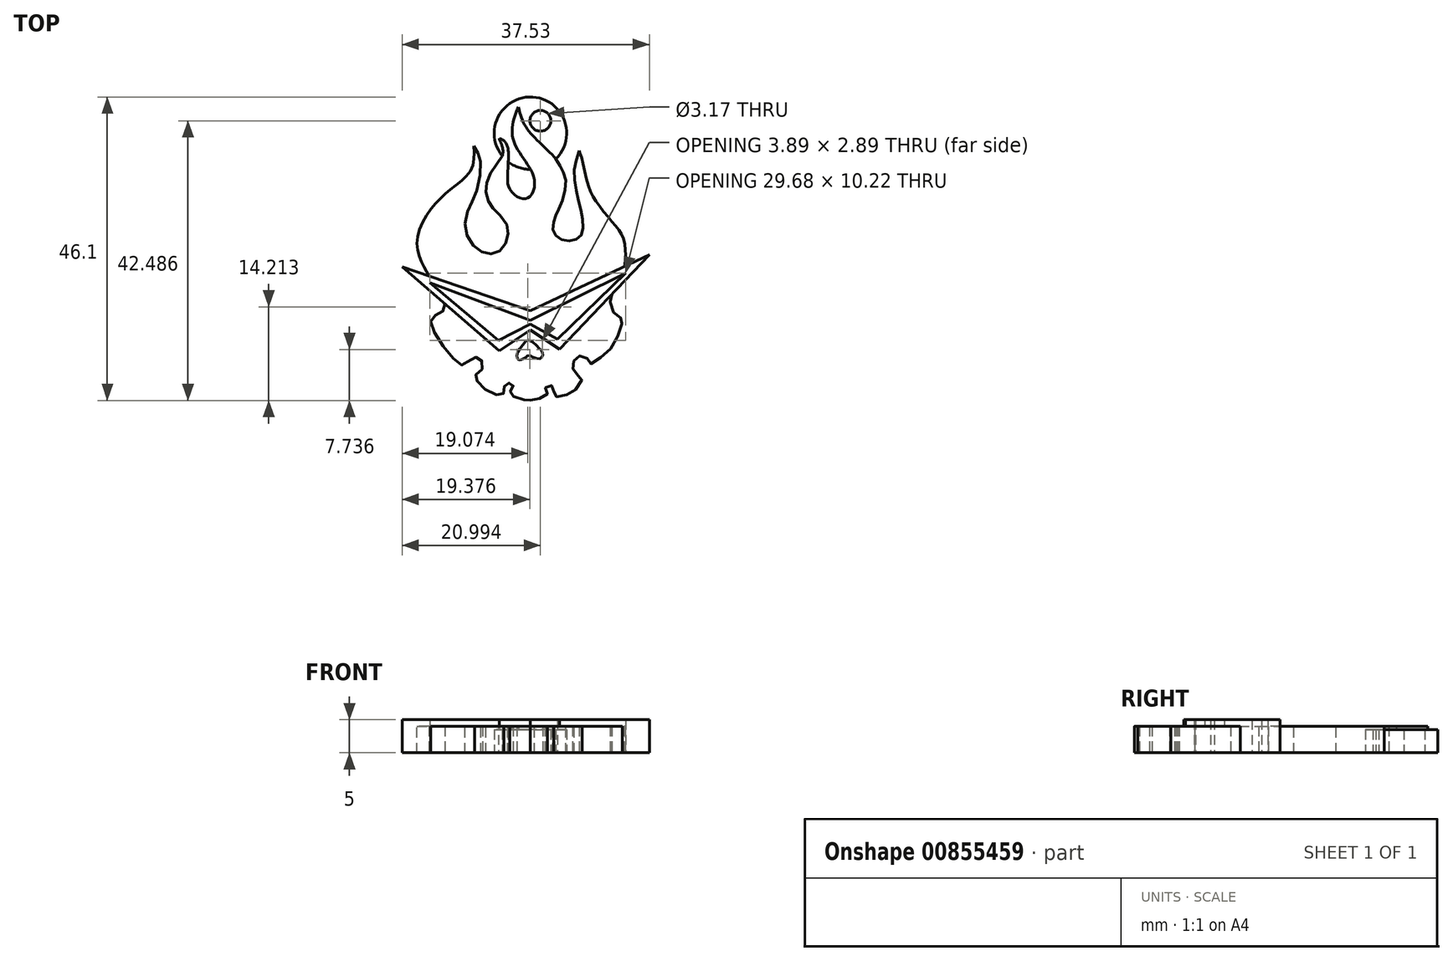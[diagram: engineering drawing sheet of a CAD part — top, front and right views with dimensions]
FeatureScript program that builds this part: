
annotation { "Feature Type Name" : "Feature", "Feature Type Description" : "" }
export const myFeature = defineFeature(function(context is Context, id is Id, definition is map)
    precondition{}
    {
        {
            var Q0;
            Q0=qCreatedBy(makeId("Top.planeOp"),FACE);
            var sketch = newSketch(context, id + "F0", { "sketchPlane" : qUnion([Q0])});
            skLineSegment(sketch, "E0", {"start": v(-8.05, -8.35) * mm, "end": v(-27.53, -1.72) * mm});
            skLineSegment(sketch, "E1", {"start": v(-27.53, -1.72) * mm, "end": v(-12.8, -14.5) * mm});
            skLineSegment(sketch, "E2", {"start": v(-12.8, -14.5) * mm, "end": v(-8.05, -11.32) * mm});
            skLineSegment(sketch, "E3", {"start": v(-8.05, -8.35) * mm, "end": v(10, 0.13) * mm});
            skLineSegment(sketch, "E4", {"start": v(10, 0.13) * mm, "end": v(-3.66, -14.25) * mm});
            skLineSegment(sketch, "E5", {"start": v(-3.66, -14.25) * mm, "end": v(-8.05, -11.32) * mm});
            skFitSpline(sketch, "E6", {"points": [v(-21.02, -7.37) * mm, v(-21.26, -8.4) * mm, v(-22.48, -9.07) * mm, v(-23.16, -9.89) * mm, v(-22.12, -12.56) * mm, v(-19.3, -16.06) * mm, v(-18.22, -16.65) * mm, v(-17.22, -15.78) * mm, v(-15.86, -15.51) * mm, v(-15.36, -16.33) * mm, v(-15.59, -17.55) * mm, v(-16.5, -18.28) * mm, v(-16, -19.23) * mm, v(-13.82, -20.96) * mm, v(-12.19, -21.05) * mm, v(-12.13, -20.46) * mm, v(-11.8, -19.54) * mm, v(-11.21, -19.35) * mm, v(-10.74, -19.62) * mm, v(-10.74, -20.15) * mm, v(-11.2, -20.78) * mm, v(-10.5, -21.49) * mm, v(-8.56, -22) * mm, v(-8.05, -21.98) * mm], "startDerivative": vector(-0.52, -28.52) * mm, "endDerivative": vector(14.8, 2.02) * mm});
            skFitSpline(sketch, "E7", {"points": [v(-8.05, -21.98) * mm, v(-6.85, -21.76) * mm, v(-5.49, -21.08) * mm, v(-5.8, -20.57) * mm, v(-5.6, -19.83) * mm, v(-4.9, -19.7) * mm, v(-4.42, -20.33) * mm, v(-4.53, -21.38) * mm, v(-3.74, -21.35) * mm, v(-2.1, -20.95) * mm, v(-0.78, -19.82) * mm, v(-0.22, -18.5) * mm, v(-0.88, -18.26) * mm, v(-1.58, -17.23) * mm, v(-1.56, -16.25) * mm, v(-0.93, -15.4) * mm, v(-0.19, -15.23) * mm, v(0.69, -15.8) * mm, v(1.01, -16.42) * mm, v(2.64, -15.46) * mm, v(4.56, -13.53) * mm, v(5.74, -10.62) * mm, v(5.84, -9.6) * mm, v(5.46, -9.38) * mm, v(4.38, -8.31) * mm, v(4.07, -6.61) * mm, v(4.29, -5.88) * mm], "startDerivative": vector(26.47, 3.3) * mm, "endDerivative": vector(8.6, 20.3) * mm});
            skFitSpline(sketch, "E8", {"points": [v(-23.45, -3.1) * mm, v(-24.64, -0.81) * mm, v(-25.22, 2.75) * mm, v(-22.84, 7.46) * mm, v(-19.9, 10.25) * mm, v(-17.04, 13.1) * mm, v(-16.65, 16.64) * mm], "startDerivative": vector(-9.07, 15.68) * mm, "endDerivative": vector(-1.26, 23.14) * mm});
            skFitSpline(sketch, "E9", {"points": [v(-16.65, 16.64) * mm, v(-16, 15.52) * mm, v(-15.6, 13.78) * mm, v(-16.4, 9.36) * mm, v(-17.39, 7.27) * mm, v(-18, 4.38) * mm, v(-17, 1.88) * mm, v(-15.27, 0.47) * mm, v(-13.57, 0.31) * mm, v(-12.1, 1.34) * mm, v(-11.49, 3) * mm, v(-11.68, 4.77) * mm, v(-13.22, 6.66) * mm, v(-14.18, 7.78) * mm, v(-14.76, 9.36) * mm, v(-14.7, 11.09) * mm, v(-13.76, 13.1) * mm, v(-12.45, 14.84) * mm, v(-12.26, 16.22) * mm, v(-12.8, 17.76) * mm], "startDerivative": vector(16.1, -26.15) * mm, "endDerivative": vector(-14.54, 32.83) * mm});
            skFitSpline(sketch, "E10", {"points": [v(-12.8, 17.76) * mm, v(-12.17, 17.54) * mm, v(-11.58, 16.64) * mm, v(-11.4, 15.18) * mm, v(-11.52, 11.79) * mm, v(-11.36, 10.47) * mm, v(-10.43, 9.23) * mm, v(-9.14, 8.64) * mm, v(-8.3, 8.84) * mm, v(-7.55, 9.97) * mm, v(-7.55, 11.92) * mm, v(-8.55, 13.9) * mm, v(-10.27, 16.64) * mm, v(-10.84, 18.66) * mm, v(-10.52, 20.93) * mm, v(-9.89, 22.56) * mm], "startDerivative": vector(15.58, -2.77) * mm, "endDerivative": vector(10.1, 22.63) * mm});
            skFitSpline(sketch, "E11", {"points": [v(-9.89, 22.56) * mm, v(-9.55, 21.27) * mm, v(-8.68, 19.43) * mm, v(-7.05, 17.55) * mm, v(-4.58, 15.1) * mm, v(-3.38, 13.3) * mm, v(-2.67, 11.02) * mm, v(-3.63, 7.32) * mm, v(-4.37, 5.66) * mm, v(-4.6, 3.83) * mm, v(-3.63, 2.56) * mm, v(-1.6, 2.29) * mm, v(-0.3, 3.17) * mm, v(-0.16, 5.42) * mm, v(-0.84, 8.7) * mm, v(-1.43, 12.51) * mm, v(-0.68, 15.92) * mm], "startDerivative": vector(5.93, -26.52) * mm, "endDerivative": vector(14.27, 44.27) * mm});
            skFitSpline(sketch, "E12", {"points": [v(-0.68, 15.92) * mm, v(-0.3, 14.83) * mm, v(0.73, 10.59) * mm, v(2, 8.1) * mm, v(4.2, 5.32) * mm, v(5.67, 3.37) * mm, v(6.33, 1.24) * mm, v(6.3, -1) * mm, v(6.2, -1.65) * mm], "startDerivative": vector(4.14, -9.55) * mm, "endDerivative": vector(-1.5, -8.02) * mm});
            skLineSegment(sketch, "E13", {"start": v(-8.05, -9.86) * mm, "end": v(-23.3, -4.14) * mm});
            skLineSegment(sketch, "E14", {"start": v(-23.3, -4.14) * mm, "end": v(-12.92, -12.9) * mm});
            skLineSegment(sketch, "E15", {"start": v(-12.92, -12.9) * mm, "end": v(-8.05, -10.43) * mm});
            skLineSegment(sketch, "E16", {"start": v(-8.05, -10.43) * mm, "end": v(-3.95, -12.68) * mm});
            skLineSegment(sketch, "E17", {"start": v(-3.95, -12.68) * mm, "end": v(6.38, -2.69) * mm});
            skLineSegment(sketch, "E18", {"start": v(6.38, -2.69) * mm, "end": v(-8.05, -9.86) * mm});
            skArc(sketch, "E19", {"start": v(-11.42, 14.24) * mm, "mid": v(-9.83, 13.38) * mm, "end": v(-8.04, 13.09) * mm});
            skCircle(sketch, "E20", {"center": v(-6.54, 20.48) * mm, "radius": 1.59 * mm});
            skArc(sketch, "E21.trimOffspring", {"start": v(-4.21, 14.65) * mm, "mid": v(-7.72, 24.08) * mm, "end": v(-12.33, 15.13) * mm});
            skFitSpline(sketch, "E22", {"points": [v(-8.24, -12.83) * mm, v(-9.37, -13.73) * mm, v(-10.07, -14.93) * mm, v(-10.03, -15.67) * mm, v(-9.65, -15.88) * mm, v(-9.36, -15.74) * mm, v(-8.82, -15.47) * mm, v(-8.44, -15.18) * mm, v(-7.67, -15.4) * mm, v(-6.6, -15.68) * mm, v(-6.24, -15.22) * mm, v(-6.21, -14.97) * mm, v(-6.42, -14.37) * mm, v(-6.92, -13.9) * mm, v(-8.24, -12.83) * mm]});
            skSolve(sketch);
        }
        {
            var Q0;
            {var subQ15=sQuery(id+"F0.wireOp",EDGE,"E8");Q0=makeQuery(id+"F0.imprint","IMPRINT",FACE,{"disambiguationData":[TD([[makeQuery(id+"F0.imprint","IMPRINT",EDGE,{"derivedFrom":subQ15}),-1.0]])]});}
            var Q1;
            {var subQ1=sQuery(id+"F0.wireOp",EDGE,"E2");Q1=makeQuery(id+"F0.imprint","IMPRINT",FACE,{"disambiguationData":[TD([[makeQuery(id+"F0.imprint","IMPRINT",EDGE,{"derivedFrom":subQ1}),-1.0]])]});}
            extrude(context, id + "F1", {"entities" : qUnion([Q0, Q1]), "depth" : 4 * mm, "offsetDistance" : 25 * mm});
        }
        {
            var Q0;
            {var subQ4=sQuery(id+"F0.wireOp",EDGE,"E19");Q0=makeQuery(id+"F0.imprint","IMPRINT",FACE,{"disambiguationData":[TD([[makeQuery(id+"F0.imprint","IMPRINT",EDGE,{"derivedFrom":subQ4}),1.0]])]});}
            extrude(context, id + "F2", {"entities" : qUnion([Q0]), "operationType" : NewBodyOperationType.ADD, "depth" : 3.5 * mm, "offsetDistance" : 25 * mm});
        }
        {
            var Q0;
            {var subQ8=sQuery(id+"F0.wireOp",EDGE,"E2");Q0=makeQuery(id+"F0.imprint","IMPRINT",FACE,{"disambiguationData":[TD([[makeQuery(id+"F0.imprint","IMPRINT",EDGE,{"derivedFrom":subQ8}),1.0]])]});}
            extrude(context, id + "F3", {"entities" : qUnion([Q0]), "operationType" : NewBodyOperationType.ADD, "depth" : 5 * mm, "offsetDistance" : 25 * mm});
        }
    });
